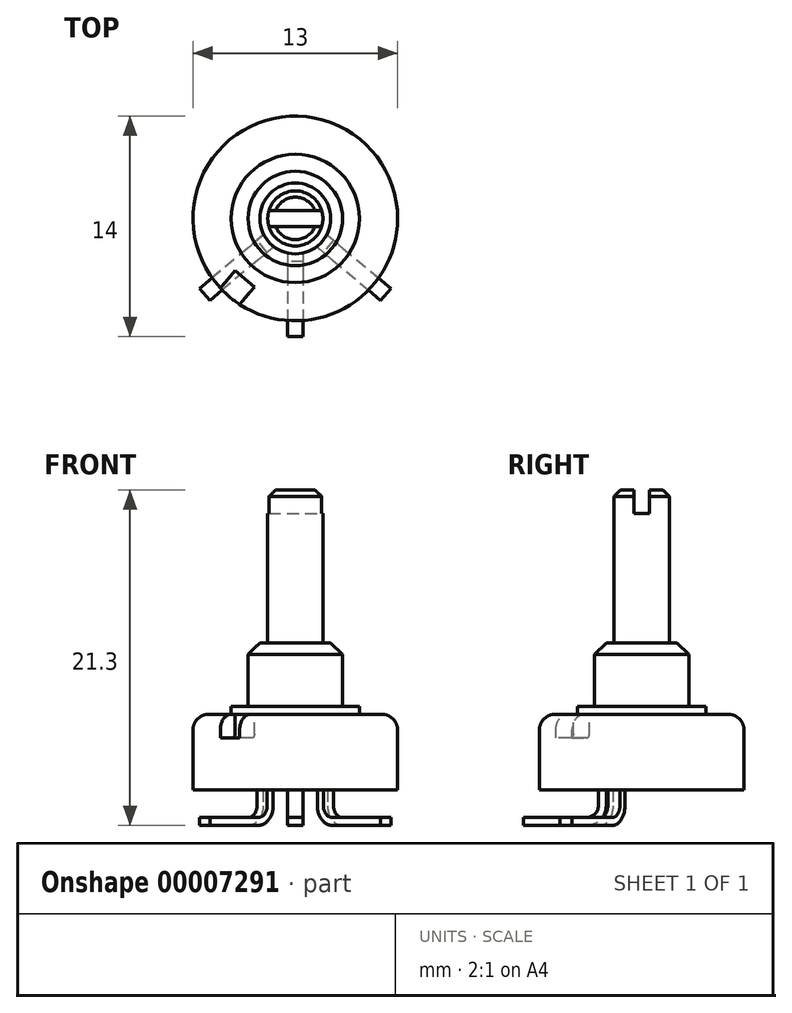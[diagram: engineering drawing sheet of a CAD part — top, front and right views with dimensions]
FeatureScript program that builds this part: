
annotation { "Feature Type Name" : "Feature", "Feature Type Description" : "" }
export const myFeature = defineFeature(function(context is Context, id is Id, definition is map)
    precondition{}
    {
        {
            var Q0;
            Q0=qCreatedBy(makeId("Top.planeOp"),FACE);
            var sketch = newSketch(context, id + "F0", { "sketchPlane" : qUnion([Q0])});
            skCircle(sketch, "E0", {"center": v(0, 0) * mm, "radius": 6.5 * mm});
            skSolve(sketch);
        }
        {
            var Q0;
            Q0 = qSketchRegion(id + "F0", true);
            extrude(context, id + "F1", {"entities" : qUnion([Q0]), "oppositeDirection" : true, "depth" : 4.8 * mm});
        }
        {
            var Q0;
            Q0=qCreatedBy(makeId("Front.planeOp"),FACE);
            var sketch = newSketch(context, id + "F2", { "sketchPlane" : qUnion([Q0])});
            skLineSegment(sketch, "E1", {"start": v(0, 0) * mm, "end": v(0, 14.25) * mm});
            skLineSegment(sketch, "E2", {"start": v(0, 14.25) * mm, "end": v(1.75, 14.25) * mm});
            skLineSegment(sketch, "E3", {"start": v(1.75, 14.25) * mm, "end": v(1.75, 4.55) * mm});
            skLineSegment(sketch, "E4", {"start": v(1.75, 4.55) * mm, "end": v(3, 4.55) * mm});
            skLineSegment(sketch, "E5", {"start": v(3, 4.55) * mm, "end": v(3, 0.5) * mm});
            skLineSegment(sketch, "E6", {"start": v(3, 0.5) * mm, "end": v(4.08, 0.5) * mm});
            skLineSegment(sketch, "E7", {"start": v(4.08, 0.5) * mm, "end": v(4.08, 0) * mm});
            skLineSegment(sketch, "E8", {"start": v(4.08, 0) * mm, "end": v(0, 0) * mm});
            skSolve(sketch);
        }
        {
            var Q0;
            Q0 = qSketchRegion(id + "F2", true);
            var Q1;
            Q1=sQuery(id+"F2.wireOp",EDGE,"E1");
            revolve(context, id + "F3", {"operationType" : NewBodyOperationType.ADD, "entities" : qUnion([Q0]), "axis" : qUnion([Q1]), "revolveType" : RevolveType.FULL});
        }
        {
            var Q0;
            Q0=makeQuery(id+"F1.opExtrude","CAP_FACE",FACE,{"disambiguationData":[OSD([sQuery(id+"F0.wireOp",EDGE,"E0")])],"isStart":true});
            var sketch = newSketch(context, id + "F4", { "sketchPlane" : qUnion([Q0])});
            skLineSegment(sketch, "E9", {"start": v(-4.76, -4.43) * mm, "end": v(-3.83, -3.32) * mm});
            skLineSegment(sketch, "E10", {"start": v(-3.83, -3.32) * mm, "end": v(-2.6, -4.34) * mm});
            skLineSegment(sketch, "E11", {"start": v(-2.6, -4.34) * mm, "end": v(-3.53, -5.46) * mm});
            skLineSegment(sketch, "E12", {"start": v(-3.21, -3.83) * mm, "end": v(0, 0) * mm, "construction": true});
            skLineSegment(sketch, "E13", {"start": v(-3.21, -3.83) * mm, "end": v(-4.18, -4.98) * mm, "construction": true});
            skLineSegment(sketch, "E14", {"start": v(0, 0) * mm, "end": v(0, -6.5) * mm, "construction": true});
            skSolve(sketch);
        }
        {
            var Q0;
            Q0 = qSketchRegion(id + "F4", true);
            var Q1;
            {var subQ2=sQuery(id+"F4.wireOp",EDGE,"E9");Q1=makeQuery(id+"F4.imprint","IMPRINT",FACE,{"disambiguationData":[TD([[makeQuery(id+"F4.imprint","IMPRINT",EDGE,{"derivedFrom":subQ2}),-1.0]])]});}
            extrude(context, id + "F5", {"entities" : qUnion([Q0, Q1]), "operationType" : NewBodyOperationType.REMOVE, "oppositeDirection" : true, "depth" : 1.5 * mm});
        }
        {
            var Q0;
            Q0=makeQuery(id+"F1.opExtrude","CAP_EDGE",EDGE,{"disambiguationData":[OSD([sQuery(id+"F0.wireOp",EDGE,"E0")])],"isStart":true});
            fillet(context, id + "F6", {"entities" : qUnion([Q0]), "radius" : 1 * mm, "tangentPropagation" : true, "allowEdgeOverflow" : false});
        }
        {
            var Q0;
            Q0=makeQuery(id+"F5.boolean.opBoolean","COPY",EDGE,{"derivedFrom":makeQuery(id+"F5.opExtrude","CAP_EDGE",EDGE,{"disambiguationData":[OSD([sQuery(id+"F4.wireOp",EDGE,"E10")])],"isStart":true})});
            var Q1;
            Q1=makeQuery(id+"F5.boolean.opBoolean","COPY",EDGE,{"derivedFrom":makeQuery(id+"F5.opExtrude","CAP_EDGE",EDGE,{"disambiguationData":[OSD([sQuery(id+"F4.wireOp",EDGE,"E10")])],"isStart":false})});
            var Q2;
            Q2=makeQuery(id+"F5.boolean.opBoolean","COPY",EDGE,{"derivedFrom":makeQuery(id+"F5.opExtrude","CAP_EDGE",EDGE,{"disambiguationData":[OSD([sQuery(id+"F0.wireOp",EDGE,"E0")])],"isStart":false})});
            fillet(context, id + "F7", {"entities" : qUnion([Q0, Q1, Q2]), "radius" : .25 * mm, "tangentPropagation" : true, "allowEdgeOverflow" : false});
        }
        {
            var Q0;
            Q0=makeQuery(id+"F3.opRevolve","SWEPT_FACE",FACE,{"disambiguationData":[OSD([sQuery(id+"F2.wireOp",EDGE,"E2")])]});
            var sketch = newSketch(context, id + "F8", { "sketchPlane" : qUnion([Q0])});
            skLineSegment(sketch, "E15", {"start": v(0, 0.5) * mm, "end": v(0, -0.5) * mm, "construction": true});
            skLineSegment(sketch, "E16", {"start": v(-1.68, 0.5) * mm, "end": v(1.68, 0.5) * mm});
            skLineSegment(sketch, "E17", {"start": v(1.68, -0.5) * mm, "end": v(-1.68, -0.5) * mm});
            skArc(sketch, "E18.0", {"start": v(-1.68, 0.5) * mm, "mid": v(-1.75, 0) * mm, "end": v(-1.68, -0.5) * mm});
            skArc(sketch, "E19.trimOffspring", {"start": v(1.68, -0.5) * mm, "mid": v(1.75, 0) * mm, "end": v(1.68, 0.5) * mm});
            skSolve(sketch);
        }
        {
            var Q0;
            Q0 = qSketchRegion(id + "F8", true);
            extrude(context, id + "F9", {"entities" : qUnion([Q0]), "operationType" : NewBodyOperationType.REMOVE, "oppositeDirection" : true, "depth" : 1.5 * mm});
        }
        {
            var Q0;
            {var subQ0=sQuery(id+"F2.wireOp",EDGE,"E2");var subQ1=sQuery(id+"F2.wireOp",EDGE,"E3");Q0=makeQuery(id+"F9.boolean.opBoolean","SPLIT",EDGE,{"disambiguationData":[TD([makeQuery(id+"F9.opExtrude","SWEPT_FACE",FACE,{"disambiguationData":[OSD([sQuery(id+"F8.wireOp",EDGE,"E17")])]})])],"derivedFrom":makeQuery(id+"F3.opRevolve","SWEPT_EDGE",EDGE,{"disambiguationData":[OSD([subQ0,subQ1])]})});}
            var Q1;
            {var subQ0=sQuery(id+"F2.wireOp",EDGE,"E2");var subQ1=sQuery(id+"F2.wireOp",EDGE,"E3");Q1=makeQuery(id+"F9.boolean.opBoolean","SPLIT",EDGE,{"disambiguationData":[TD([makeQuery(id+"F9.opExtrude","SWEPT_FACE",FACE,{"disambiguationData":[OSD([sQuery(id+"F8.wireOp",EDGE,"E16")])]})])],"derivedFrom":makeQuery(id+"F3.opRevolve","SWEPT_EDGE",EDGE,{"disambiguationData":[OSD([subQ0,subQ1])]})});}
            chamfer(context, id + "F10", {"entities" : qUnion([Q0, Q1]), "width" : .4 * mm, "tangentPropagation" : true});
        }
        {
            var Q0;
            Q0=makeQuery(id+"F3.opRevolve","SWEPT_EDGE",EDGE,{"disambiguationData":[OSD([sQuery(id+"F2.wireOp",EDGE,"E4"),sQuery(id+"F2.wireOp",EDGE,"E5")])]});
            chamfer(context, id + "F11", {"entities" : qUnion([Q0]), "width" : .75 * mm, "tangentPropagation" : true});
        }
        {
            var Q0;
            Q0=qCreatedBy(makeId("Right.planeOp"),FACE);
            var sketch = newSketch(context, id + "F12", { "sketchPlane" : qUnion([Q0])});
            skLineSegment(sketch, "E20.0", {"start": v(-6.5, -4.8) * mm, "end": v(6.5, -4.8) * mm, "construction": true});
            skLineSegment(sketch, "E21", {"start": v(-2.5, -4.8) * mm, "end": v(-2.5, -5.8) * mm});
            skArc(sketch, "E22", {"start": v(-2.5, -5.8) * mm, "mid": v(-2.8, -6.5) * mm, "end": v(-3.5, -6.8) * mm});
            skLineSegment(sketch, "E23", {"start": v(-3.5, -6.8) * mm, "end": v(-7.5, -6.8) * mm});
            skSolve(sketch);
        }
        {
            var Q0;
            Q0=makeQuery(id+"F1.opExtrude","CAP_FACE",FACE,{"disambiguationData":[OSD([sQuery(id+"F0.wireOp",EDGE,"E0")])],"isStart":false});
            var sketch = newSketch(context, id + "F13", { "sketchPlane" : qUnion([Q0])});
            skLineSegment(sketch, "E24.0", {"start": v(0, 3.5) * mm, "end": v(0, 7.5) * mm, "construction": true});
            skLineSegment(sketch, "E25.0", {"start": v(0, 2.5) * mm, "end": v(0, 3.5) * mm, "construction": true});
            skLineSegment(sketch, "E26.rect.bottom", {"start": v(0.5, 2.25) * mm, "end": v(-0.5, 2.25) * mm});
            skLineSegment(sketch, "E26.rect.top", {"start": v(0.5, 2.75) * mm, "end": v(-0.5, 2.75) * mm});
            skLineSegment(sketch, "E26.rect.left", {"start": v(0.5, 2.25) * mm, "end": v(0.5, 2.75) * mm});
            skLineSegment(sketch, "E26.rect.right", {"start": v(-0.5, 2.25) * mm, "end": v(-0.5, 2.75) * mm});
            skPoint(sketch, "E26.rect.middle", {"position": v(0, 2.5) * mm});
            skSolve(sketch);
        }
        {
            var Q0;
            Q0 = qSketchRegion(id + "F13", true);
            var Q1;
            Q1=sQuery(id+"F12.wireOp",EDGE,"E21");
            var Q2;
            Q2=sQuery(id+"F12.wireOp",EDGE,"E22");
            var Q3;
            Q3=sQuery(id+"F12.wireOp",EDGE,"E23");
            sweep(context, id + "F14", {"profiles" : qUnion([Q0]), "path" : qUnion([Q1, Q2, Q3])});
        }
        {
            var Q0;
            Q0=makeQuery(id+"F14.opSweep","SWEPT_BODY",BODY,{"disambiguationData":[OSD([sQuery(id+"F12.wireOp",EDGE,"E23"),sQuery(id+"F13.wireOp",EDGE,"E26.rect.bottom"),sQuery(id+"F13.wireOp",EDGE,"E26.rect.top"),sQuery(id+"F13.wireOp",EDGE,"E26.rect.left"),sQuery(id+"F13.wireOp",EDGE,"E26.rect.right")])]});
            var Q1;
            Q1=makeQuery(id+"F3.opRevolve","SWEPT_FACE",FACE,{"disambiguationData":[OSD([sQuery(id+"F2.wireOp",EDGE,"E3")])]});
            circularPattern(context, id + "F15", {"entities" : qUnion([Q0]), "axis" : qUnion([Q1]), "angle" : 50 * degree, "instanceCount" : 2});
        }
        {
            var Q0;
            Q0=makeQuery(id+"F14.opSweep","SWEPT_BODY",BODY,{"disambiguationData":[OSD([sQuery(id+"F12.wireOp",EDGE,"E23"),sQuery(id+"F13.wireOp",EDGE,"E26.rect.bottom"),sQuery(id+"F13.wireOp",EDGE,"E26.rect.top"),sQuery(id+"F13.wireOp",EDGE,"E26.rect.left"),sQuery(id+"F13.wireOp",EDGE,"E26.rect.right")])]});
            var Q1;
            Q1=makeQuery(id+"F3.opRevolve","SWEPT_FACE",FACE,{"disambiguationData":[OSD([sQuery(id+"F2.wireOp",EDGE,"E3")])]});
            circularPattern(context, id + "F16", {"entities" : qUnion([Q0]), "axis" : qUnion([Q1]), "angle" : 50 * degree, "instanceCount" : 2, "oppositeDirection" : true});
        }
    });
